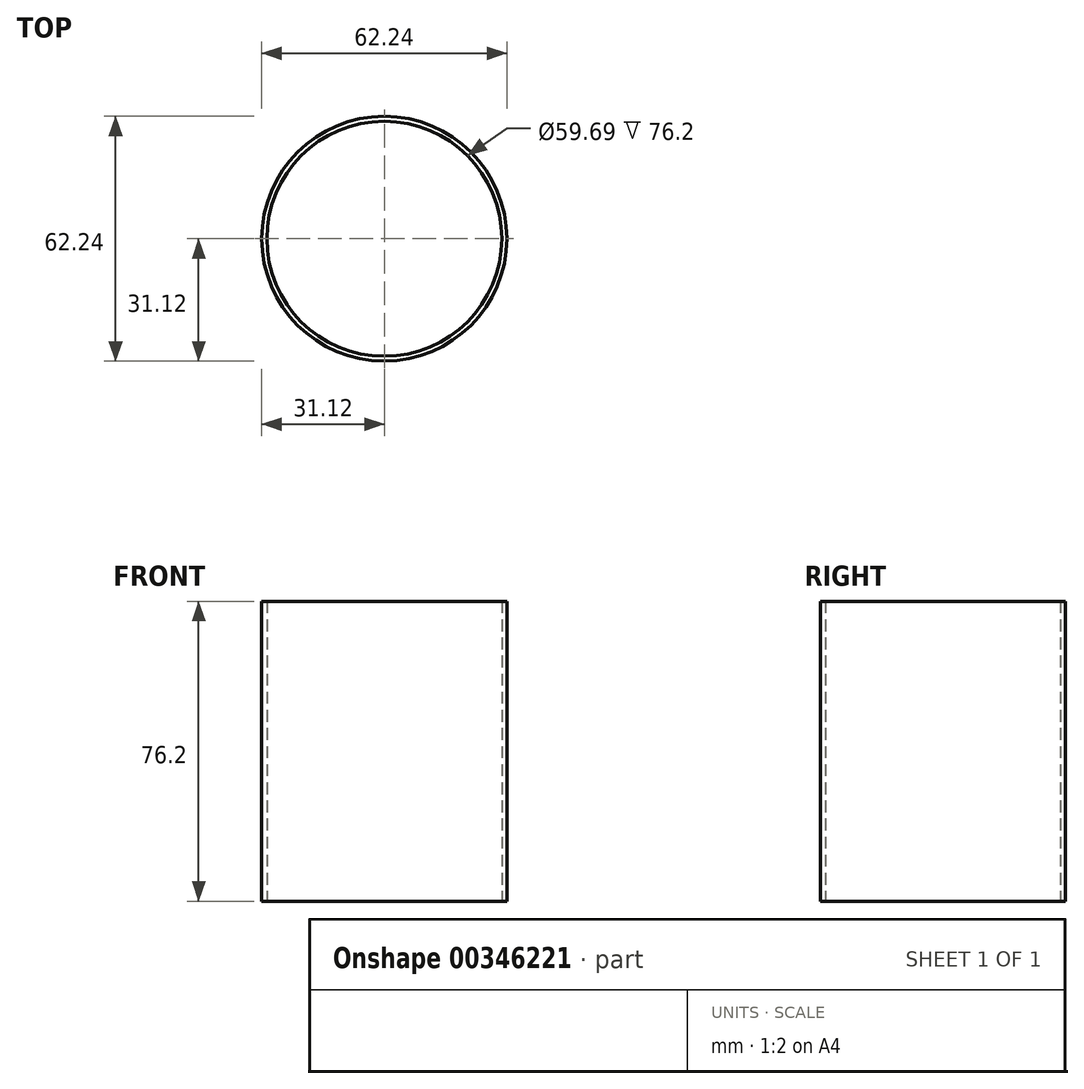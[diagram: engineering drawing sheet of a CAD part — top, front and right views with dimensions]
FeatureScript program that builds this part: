
annotation { "Feature Type Name" : "Feature", "Feature Type Description" : "" }
export const myFeature = defineFeature(function(context is Context, id is Id, definition is map)
    precondition{}
    {
        {
            var Q0;
            Q0=qCreatedBy(makeId("Top.planeOp"),FACE);
            var sketch = newSketch(context, id + "F0", { "sketchPlane" : qUnion([Q0])});
            skCircle(sketch, "E0", {"center": v(-76.2, -12.7) * mm, "radius": 26.67 * mm});
            skCircle(sketch, "E1", {"center": v(76.2, -12.7) * mm, "radius": 25.4 * mm});
            skLineSegment(sketch, "E2.bottom", {"start": v(-36.51, 13.5) * mm, "end": v(36.51, 13.5) * mm});
            skLineSegment(sketch, "E2.top", {"start": v(-36.51, -13.5) * mm, "end": v(36.51, -13.5) * mm});
            skLineSegment(sketch, "E2.left", {"start": v(-36.51, 13.5) * mm, "end": v(-36.51, -13.5) * mm});
            skLineSegment(sketch, "E2.right", {"start": v(36.51, 13.5) * mm, "end": v(36.51, -13.5) * mm});
            skPoint(sketch, "E2.middle", {"position": v(0, 0) * mm});
            skLineSegment(sketch, "E3.bottom", {"start": v(26.67, -31.75) * mm, "end": v(-1.27, -31.75) * mm});
            skLineSegment(sketch, "E3.top", {"start": v(26.67, -44.45) * mm, "end": v(-1.27, -44.45) * mm});
            skLineSegment(sketch, "E3.left", {"start": v(26.67, -31.75) * mm, "end": v(26.67, -44.45) * mm});
            skLineSegment(sketch, "E3.right", {"start": v(-1.27, -31.75) * mm, "end": v(-1.27, -44.45) * mm});
            skPoint(sketch, "E3.middle", {"position": v(12.7, -38.1) * mm});
            skCircle(sketch, "E4", {"center": v(44.45, -38.1) * mm, "radius": 4.76 * mm});
            skCircle(sketch, "E5", {"center": v(-76.2, -12.7) * mm, "radius": 29.85 * mm});
            skCircle(sketch, "E6", {"center": v(76.2, -12.7) * mm, "radius": 28.58 * mm});
            skCircle(sketch, "E7", {"center": v(-76.2, -12.7) * mm, "radius": 31.12 * mm});
            skCircle(sketch, "E8", {"center": v(76.2, -12.7) * mm, "radius": 29.85 * mm});
            skLineSegment(sketch, "E9.0", {"start": v(-39.05, 16.03) * mm, "end": v(39.05, 16.03) * mm});
            skLineSegment(sketch, "E9.1", {"start": v(-39.05, 16.03) * mm, "end": v(-39.05, -16.03) * mm});
            skLineSegment(sketch, "E9.2", {"start": v(-39.05, -16.03) * mm, "end": v(39.05, -16.03) * mm});
            skLineSegment(sketch, "E9.3", {"start": v(39.05, 16.03) * mm, "end": v(39.05, -16.03) * mm});
            skSolve(sketch);
        }
        {
            var Q0;
            Q0=makeQuery(id+"F0.imprint","IMPRINT",FACE,{"disambiguationData":[TD([[makeQuery(id+"F0.imprint","IMPRINT",EDGE,{"derivedFrom":sQuery(id+"F0.wireOp",EDGE,"E5")}),-1.0]])]});
            extrude(context, id + "F1", {"entities" : qUnion([Q0]), "depth" : 76.2 * mm});
        }
    });
